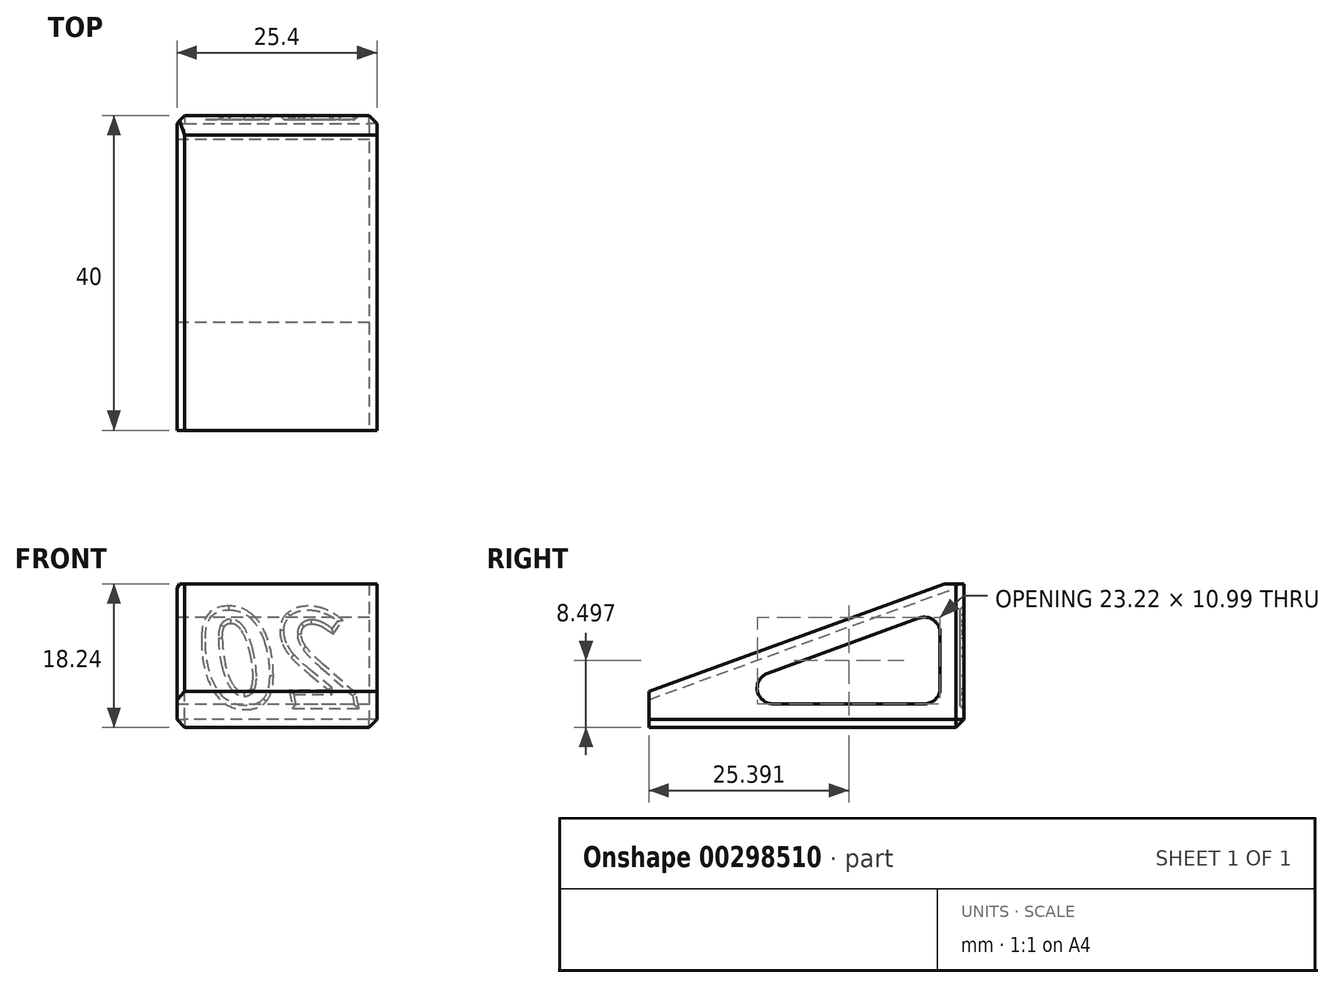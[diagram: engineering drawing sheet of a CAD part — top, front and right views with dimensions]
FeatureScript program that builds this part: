
annotation { "Feature Type Name" : "Feature", "Feature Type Description" : "" }
export const myFeature = defineFeature(function(context is Context, id is Id, definition is map)
    precondition{}
    {
        {
            var Q0;
            Q0=qCreatedBy(makeId("Top.planeOp"),FACE);
            var sketch = newSketch(context, id + "F0", { "sketchPlane" : qUnion([Q0])});
            skLineSegment(sketch, "E0.rect.bottom", {"start": v(-12.7, 20) * mm, "end": v(12.7, 20) * mm});
            skLineSegment(sketch, "E0.rect.top", {"start": v(-12.7, -20) * mm, "end": v(12.7, -20) * mm});
            skLineSegment(sketch, "E0.rect.left", {"start": v(-12.7, 20) * mm, "end": v(-12.7, -20) * mm});
            skLineSegment(sketch, "E0.rect.right", {"start": v(12.7, 20) * mm, "end": v(12.7, -20) * mm});
            skPoint(sketch, "E0.rect.middle", {"position": v(0, 0) * mm});
            skSolve(sketch);
        }
        {
            var Q0;
            Q0=qSketchRegion(id+"F0",true);
            extrude(context, id + "F1", {"entities" : qUnion([Q0]), "depth" : 25 * mm});
        }
        {
            var Q0;
            Q0=makeQuery(id+"F1.opExtrude","SWEPT_FACE",FACE,{"disambiguationData":[OSD([sQuery(id+"F0.wireOp",EDGE,"E0.rect.right")])]});
            var sketch = newSketch(context, id + "F2", { "sketchPlane" : qUnion([Q0])});
            skLineSegment(sketch, "E1", {"start": v(17.5, 18.24) * mm, "end": v(-20, 4.59) * mm});
            skLineSegment(sketch, "E2", {"start": v(-20, 0) * mm, "end": v(-20, 36.1) * mm});
            skLineSegment(sketch, "E3", {"start": v(17.5, 18.24) * mm, "end": v(20, 18.24) * mm});
            skLineSegment(sketch, "E4", {"start": v(20, 18.24) * mm, "end": v(20, 36.1) * mm});
            skLineSegment(sketch, "E5", {"start": v(20, 36.1) * mm, "end": v(-20, 36.1) * mm});
            skSolve(sketch);
        }
        {
            var Q0;
            Q0=qSketchRegion(id+"F2",true);
            extrude(context, id + "F3", {"entities" : qUnion([Q0]), "operationType" : NewBodyOperationType.REMOVE, "endBound" : BoundingType.THROUGH_ALL, "oppositeDirection" : true, "depth" : 25 * mm});
        }
        {
            var Q0;
            Q0=makeQuery(id+"F1.opExtrude","SWEPT_FACE",FACE,{"disambiguationData":[OSD([sQuery(id+"F0.wireOp",EDGE,"E0.rect.right")])]});
            var sketch = newSketch(context, id + "F4", { "sketchPlane" : qUnion([Q0])});
            skLineSegment(sketch, "E6.0", {"start": v(12, 3) * mm, "end": v(-15.6, 3) * mm});
            skLineSegment(sketch, "E6.1", {"start": v(17, 14.86) * mm, "end": v(-15.6, 3) * mm});
            skLineSegment(sketch, "E6.2", {"start": v(17, 3) * mm, "end": v(12, 3) * mm});
            skLineSegment(sketch, "E6.3", {"start": v(17, 14.86) * mm, "end": v(17, 3) * mm});
            skSolve(sketch);
        }
        {
            var Q0;
            Q0=qSketchRegion(id+"F4",true);
            extrude(context, id + "F5", {"entities" : qUnion([Q0]), "operationType" : NewBodyOperationType.REMOVE, "endBound" : BoundingType.THROUGH_ALL, "oppositeDirection" : true, "depth" : 25 * mm});
        }
        {
            var Q0;
            Q0=makeQuery(id+"F5.boolean.opBoolean","COPY",EDGE,{"derivedFrom":makeQuery(id+"F5.opExtrude","SWEPT_EDGE",EDGE,{"disambiguationData":[OSD([sQuery(id+"F4.wireOp",EDGE,"E6.3"),sQuery(id+"F4.wireOp",EDGE,"E6.4")])]})});
            var Q1;
            Q1=makeQuery(id+"F5.boolean.opBoolean","COPY",EDGE,{"derivedFrom":makeQuery(id+"F5.opExtrude","SWEPT_EDGE",EDGE,{"disambiguationData":[OSD([sQuery(id+"F4.wireOp",EDGE,"E6.0"),sQuery(id+"F4.wireOp",EDGE,"E6.1")])]})});
            var Q2;
            Q2=makeQuery(id+"F5.boolean.opBoolean","COPY",EDGE,{"derivedFrom":makeQuery(id+"F5.opExtrude","SWEPT_EDGE",EDGE,{"disambiguationData":[OSD([sQuery(id+"F4.wireOp",EDGE,"E6.2"),sQuery(id+"F4.wireOp",EDGE,"E6.3")])]})});
            fillet(context, id + "F6", {"entities" : qUnion([Q0, Q1, Q2]), "radius" : 2 * mm, "tangentPropagation" : true, "allowEdgeOverflow" : false});
        }
        {
            var Q0;
            Q0=makeQuery(id+"F1.opExtrude","SWEPT_FACE",FACE,{"disambiguationData":[OSD([sQuery(id+"F0.wireOp",EDGE,"E0.rect.bottom")])]});
            var sketch = newSketch(context, id + "F7", { "sketchPlane" : qUnion([Q0])});
            skText(sketch, "E7", { "text": "20", "fontName": "OpenSans-BoldItalic.ttf"});
            const initialGuessF7  = {"E7": [-0.01, 0.00244, 1, 0, 0.0129]};
            skSetInitialGuess(sketch, initialGuessF7);
            skSolve(sketch);
        }
        {
            var Q0;
            Q0=qSketchRegion(id+"F7",true);
            extrude(context, id + "F8", {"entities" : qUnion([Q0]), "operationType" : NewBodyOperationType.REMOVE, "oppositeDirection" : true, "depth" : .5 * mm});
        }
        {
            var Q0;
            Q0=makeQuery(id+"F8.boolean.opBoolean","COPY",FACE,{"derivedFrom":makeQuery(id+"F8.opExtrude","CAP_FACE",FACE,{"disambiguationData":[OSD([sQuery(id+"F7.wireOp",EDGE,"E7.sketch_text.stroke-0"),sQuery(id+"F7.wireOp",EDGE,"E7.sketch_text.stroke-1"),sQuery(id+"F7.wireOp",EDGE,"E7.sketch_text.stroke-2"),sQuery(id+"F7.wireOp",EDGE,"E7.sketch_text.stroke-3"),sQuery(id+"F7.wireOp",EDGE,"E7.sketch_text.stroke-4"),sQuery(id+"F7.wireOp",EDGE,"E7.sketch_text.stroke-5"),sQuery(id+"F7.wireOp",EDGE,"E7.sketch_text.stroke-6"),sQuery(id+"F7.wireOp",EDGE,"E7.sketch_text.stroke-7"),sQuery(id+"F7.wireOp",EDGE,"E7.sketch_text.stroke-8"),sQuery(id+"F7.wireOp",EDGE,"E7.sketch_text.stroke-9"),sQuery(id+"F7.wireOp",EDGE,"E7.sketch_text.stroke-10"),sQuery(id+"F7.wireOp",EDGE,"E7.sketch_text.stroke-11"),sQuery(id+"F7.wireOp",EDGE,"E7.sketch_text.stroke-12"),sQuery(id+"F7.wireOp",EDGE,"E7.sketch_text.stroke-13"),sQuery(id+"F7.wireOp",EDGE,"E7.sketch_text.stroke-14"),sQuery(id+"F7.wireOp",EDGE,"E7.sketch_text.stroke-15"),sQuery(id+"F7.wireOp",EDGE,"E7.sketch_text.stroke-16"),sQuery(id+"F7.wireOp",EDGE,"E7.sketch_text.stroke-17"),sQuery(id+"F7.wireOp",EDGE,"E7.sketch_text.stroke-18"),sQuery(id+"F7.wireOp",EDGE,"E7.sketch_text.stroke-19"),sQuery(id+"F7.wireOp",EDGE,"E7.sketch_text.stroke-20"),sQuery(id+"F7.wireOp",EDGE,"E7.sketch_text.stroke-21"),sQuery(id+"F7.wireOp",EDGE,"E7.sketch_text.stroke-22"),sQuery(id+"F7.wireOp",EDGE,"E7.sketch_text.stroke-23"),sQuery(id+"F7.wireOp",EDGE,"E7.sketch_text.stroke-24"),sQuery(id+"F7.wireOp",EDGE,"E7.sketch_text.stroke-25"),sQuery(id+"F7.wireOp",EDGE,"E7.sketch_text.stroke-26"),sQuery(id+"F7.wireOp",EDGE,"E7.sketch_text.stroke-27")])],"isStart":false})});
            var Q1;
            Q1=makeQuery(id+"F8.boolean.opBoolean","COPY",FACE,{"derivedFrom":makeQuery(id+"F8.opExtrude","CAP_FACE",FACE,{"disambiguationData":[OSD([sQuery(id+"F7.wireOp",EDGE,"E7.sketch_text.stroke-28"),sQuery(id+"F7.wireOp",EDGE,"E7.sketch_text.stroke-29"),sQuery(id+"F7.wireOp",EDGE,"E7.sketch_text.stroke-30"),sQuery(id+"F7.wireOp",EDGE,"E7.sketch_text.stroke-31"),sQuery(id+"F7.wireOp",EDGE,"E7.sketch_text.stroke-32"),sQuery(id+"F7.wireOp",EDGE,"E7.sketch_text.stroke-33"),sQuery(id+"F7.wireOp",EDGE,"E7.sketch_text.stroke-34"),sQuery(id+"F7.wireOp",EDGE,"E7.sketch_text.stroke-35"),sQuery(id+"F7.wireOp",EDGE,"E7.sketch_text.stroke-36"),sQuery(id+"F7.wireOp",EDGE,"E7.sketch_text.stroke-37"),sQuery(id+"F7.wireOp",EDGE,"E7.sketch_text.stroke-38"),sQuery(id+"F7.wireOp",EDGE,"E7.sketch_text.stroke-39"),sQuery(id+"F7.wireOp",EDGE,"E7.sketch_text.stroke-40"),sQuery(id+"F7.wireOp",EDGE,"E7.sketch_text.stroke-41"),sQuery(id+"F7.wireOp",EDGE,"E7.sketch_text.stroke-42"),sQuery(id+"F7.wireOp",EDGE,"E7.sketch_text.stroke-43"),sQuery(id+"F7.wireOp",EDGE,"E7.sketch_text.stroke-44"),sQuery(id+"F7.wireOp",EDGE,"E7.sketch_text.stroke-45")])],"isStart":false})});
            chamfer(context, id + "F9", {"entities" : qUnion([Q0, Q1]), "width" : .5 * mm, "tangentPropagation" : true});
        }
        {
            var Q0;
            Q0=makeQuery(id+"F1.opExtrude","SWEPT_EDGE",EDGE,{"disambiguationData":[OSD([sQuery(id+"F0.wireOp",EDGE,"E0.rect.bottom"),sQuery(id+"F0.wireOp",EDGE,"E0.rect.right")])]});
            var Q1;
            Q1=makeQuery(id+"F1.opExtrude","CAP_EDGE",EDGE,{"disambiguationData":[OSD([sQuery(id+"F0.wireOp",EDGE,"E0.rect.bottom")])],"isStart":false});
            var Q2;
            Q2=makeQuery(id+"F1.opExtrude","SWEPT_EDGE",EDGE,{"disambiguationData":[OSD([sQuery(id+"F0.wireOp",EDGE,"E0.rect.bottom"),sQuery(id+"F0.wireOp",EDGE,"E0.rect.left")])]});
            var Q3;
            Q3=makeQuery(id+"F1.opExtrude","CAP_EDGE",EDGE,{"disambiguationData":[OSD([sQuery(id+"F0.wireOp",EDGE,"E0.rect.bottom")])],"isStart":true});
            var Q4;
            Q4=makeQuery(id+"F1.opExtrude","CAP_EDGE",EDGE,{"disambiguationData":[OSD([sQuery(id+"F0.wireOp",EDGE,"E0.rect.right")])],"isStart":true});
            var Q5;
            Q5=makeQuery(id+"F1.opExtrude","CAP_EDGE",EDGE,{"disambiguationData":[OSD([sQuery(id+"F0.wireOp",EDGE,"E0.rect.left")])],"isStart":true});
            var Q6;
            Q6=makeQuery(id+"F3.boolean.opBoolean","COPY",EDGE,{"derivedFrom":makeQuery(id+"F3.opExtrude","CAP_EDGE",EDGE,{"disambiguationData":[OSD([sQuery(id+"F2.wireOp",EDGE,"E1")])],"isStart":true})});
            var Q7;
            Q7=makeQuery(id+"F3.boolean.opBoolean","INTERSECT",EDGE,{"derivedFrom":[makeQuery(id+"F1.opExtrude","SWEPT_FACE",FACE,{"disambiguationData":[OSD([sQuery(id+"F0.wireOp",EDGE,"E0.rect.left")])]}),makeQuery(id+"F3.opExtrude","SWEPT_FACE",FACE,{"disambiguationData":[OSD([sQuery(id+"F2.wireOp",EDGE,"E1")])]})]});
            var Q8;
            Q8=makeQuery(id+"F3.boolean.opBoolean","COPY",EDGE,{"derivedFrom":makeQuery(id+"F3.opExtrude","SWEPT_EDGE",EDGE,{"disambiguationData":[OSD([sQuery(id+"F0.wireOp",EDGE,"E0.rect.bottom"),sQuery(id+"F0.wireOp",EDGE,"E0.rect.right"),sQuery(id+"F2.wireOp",EDGE,"E3"),sQuery(id+"F2.wireOp",EDGE,"E4")])]})});
            chamfer(context, id + "F10", {"entities" : qUnion([Q0, Q1, Q2, Q3, Q4, Q5, Q6, Q7, Q8]), "width" : 1 * mm, "tangentPropagation" : true});
        }
    });
